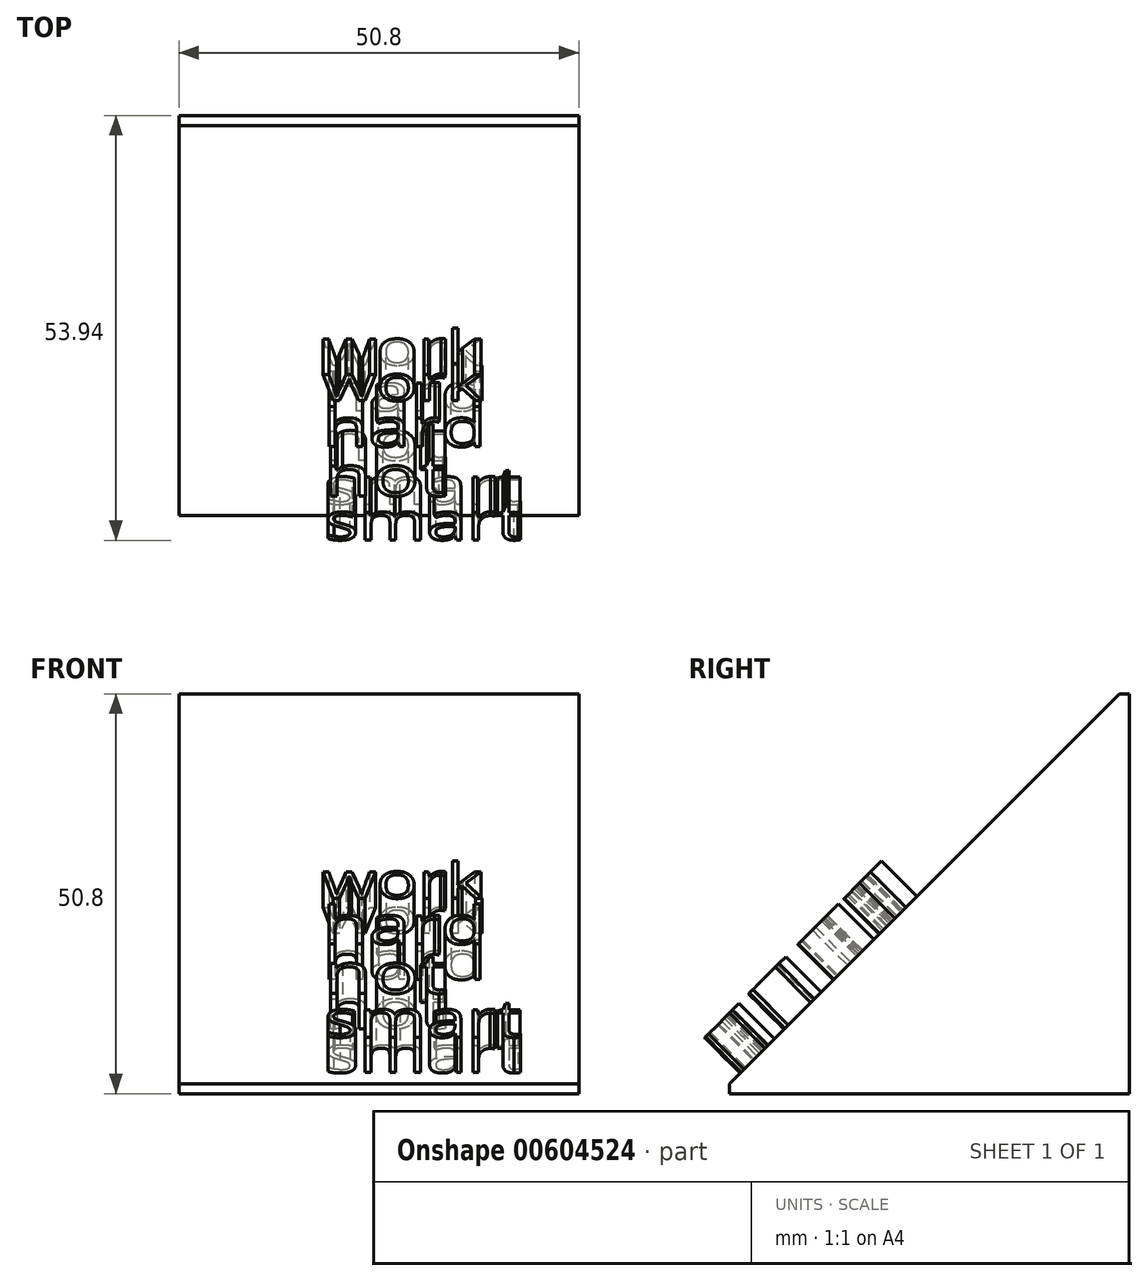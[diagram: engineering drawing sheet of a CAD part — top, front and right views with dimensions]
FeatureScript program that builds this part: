
annotation { "Feature Type Name" : "Feature", "Feature Type Description" : "" }
export const myFeature = defineFeature(function(context is Context, id is Id, definition is map)
    precondition{}
    {
        {
            var Q0;
            Q0=qCreatedBy(makeId("Top.planeOp"),FACE);
            var sketch = newSketch(context, id + "F0", { "sketchPlane" : qUnion([Q0])});
            skLineSegment(sketch, "E0.bottom", {"start": v(-25.4, 25.4) * mm, "end": v(25.4, 25.4) * mm});
            skLineSegment(sketch, "E0.top", {"start": v(-25.4, -25.4) * mm, "end": v(25.4, -25.4) * mm});
            skLineSegment(sketch, "E0.left", {"start": v(-25.4, 25.4) * mm, "end": v(-25.4, -25.4) * mm});
            skLineSegment(sketch, "E0.right", {"start": v(25.4, 25.4) * mm, "end": v(25.4, -25.4) * mm});
            skSolve(sketch);
        }
        {
            var Q0;
            Q0=makeQuery(id+"F0.imprint","IMPRINT",FACE,{"disambiguationData":[TD([[makeQuery(id+"F0.imprint","IMPRINT",EDGE,{"derivedFrom":sQuery(id+"F0.wireOp",EDGE,"E0.bottom")}),-1.0]])]});
            extrude(context, id + "F1", {"entities" : qUnion([Q0]), "depth" : 50.8 * mm, "offsetDistance" : 25.4 * mm});
        }
        {
            var Q0;
            Q0=makeQuery(id+"F1.opExtrude","CAP_EDGE",EDGE,{"disambiguationData":[OSD([sQuery(id+"F0.wireOp",EDGE,"E0.top")])],"isStart":false});
            chamfer(context, id + "F2", {"entities" : qUnion([Q0]), "width" : 49.53 * mm, "tangentPropagation" : true});
        }
        {
            var Q0;
            Q0=makeQuery(id+"F2.opChamfer","BLEND_FACE",FACE,{"disambiguationData":[OSD([sQuery(id+"F0.wireOp",EDGE,"E0.top")])]});
            var sketch = newSketch(context, id + "F3", { "sketchPlane" : qUnion([Q0])});
            skText(sketch, "E1", { "text": "work", "fontName": "OpenSans-Regular.ttf"});
            skText(sketch, "E2", { "text": "hard", "fontName": "OpenSans-Regular.ttf"});
            skText(sketch, "E3", { "text": "not", "fontName": "OpenSans-Regular.ttf"});
            skText(sketch, "E4", { "text": "smart", "fontName": "OpenSans-Regular.ttf"});
            const initialGuessF3  = {"E1": [-0.0072, 0.00991, 1, 0, 0.00635], "E2": [-0.00713, 0.00168, 1, 0, 0.00684], "E3": [-0.00699, -0.00718, 1, 0, 0.00718], "E4": [-0.00692, -0.01507, 1, 0, 0.00663]};
            skSetInitialGuess(sketch, initialGuessF3);
            skSolve(sketch);
        }
        {
            var Q0;
            Q0 = qSketchRegion(id + "F3", true);
            extrude(context, id + "F4", {"entities" : qUnion([Q0]), "operationType" : NewBodyOperationType.ADD, "depth" : 6.35 * mm, "offsetDistance" : 25.4 * mm});
        }
    });
